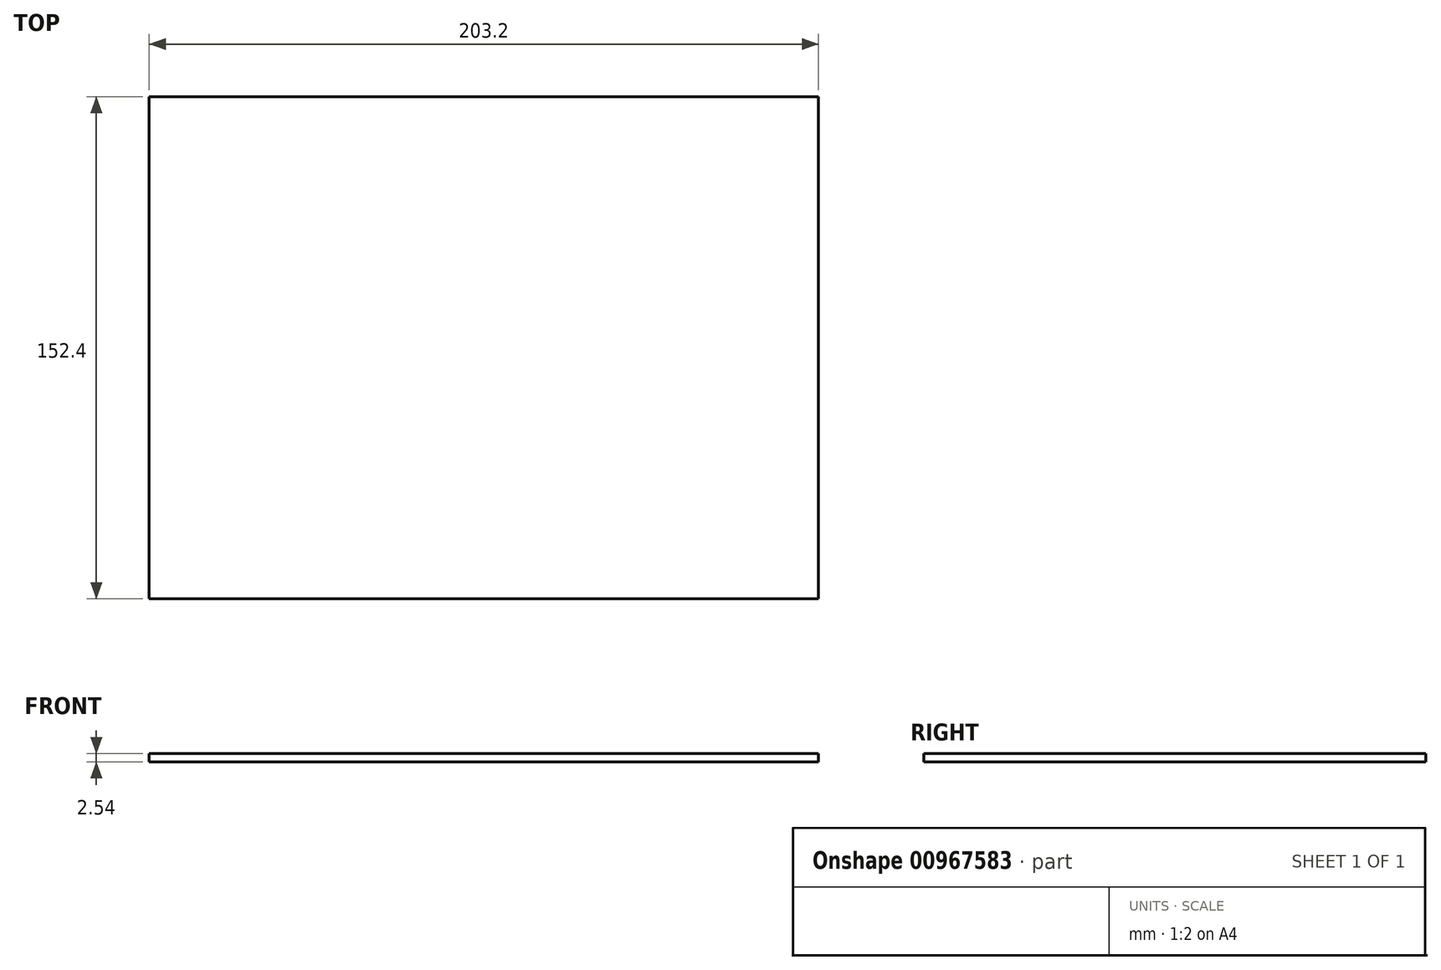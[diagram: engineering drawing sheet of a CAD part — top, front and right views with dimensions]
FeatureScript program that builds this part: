
annotation { "Feature Type Name" : "Feature", "Feature Type Description" : "" }
export const myFeature = defineFeature(function(context is Context, id is Id, definition is map)
    precondition{}
    {
        {
            var Q0;
            Q0=qCreatedBy(makeId("Top.planeOp"),FACE);
            var sketch = newSketch(context, id + "F0", { "sketchPlane" : qUnion([Q0])});
            skLineSegment(sketch, "E0.bottom", {"start": v(0, 152.4) * mm, "end": v(203.2, 152.4) * mm});
            skLineSegment(sketch, "E0.top", {"start": v(0, 0) * mm, "end": v(203.2, 0) * mm});
            skLineSegment(sketch, "E0.left", {"start": v(0, 152.4) * mm, "end": v(0, 0) * mm});
            skLineSegment(sketch, "E0.right", {"start": v(203.2, 152.4) * mm, "end": v(203.2, 0) * mm});
            skSolve(sketch);
        }
        {
            var Q0;
            Q0 = qSketchRegion(id + "F0", true);
            extrude(context, id + "F1", {"entities" : qUnion([Q0]), "depth" : 2.54 * mm, "offsetDistance" : 25.4 * mm});
        }
    });
